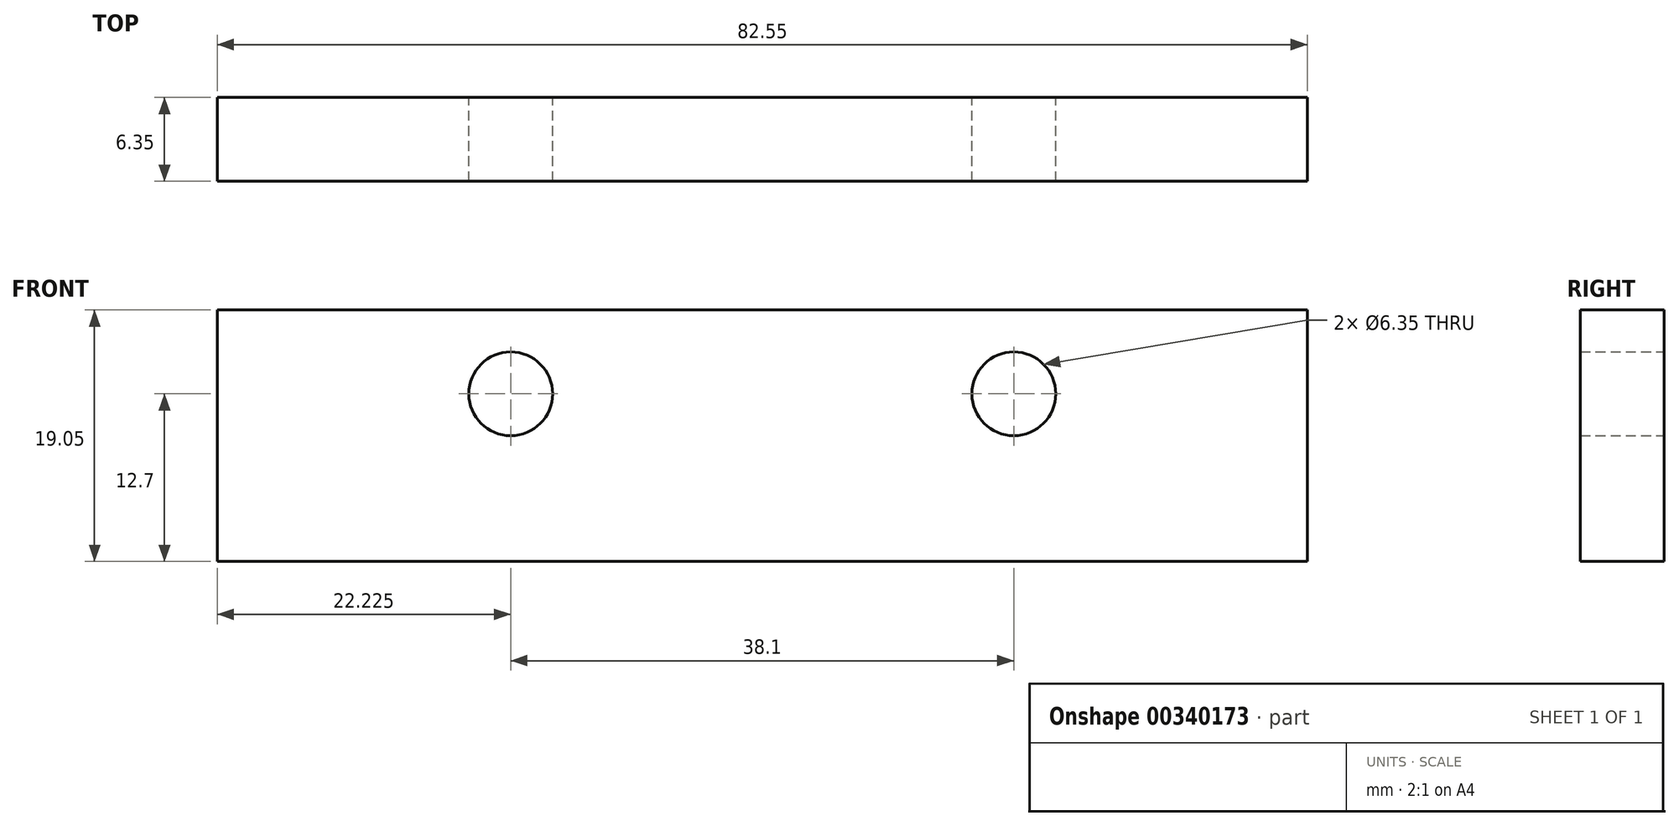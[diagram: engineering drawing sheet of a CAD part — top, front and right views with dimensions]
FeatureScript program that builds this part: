
annotation { "Feature Type Name" : "Feature", "Feature Type Description" : "" }
export const myFeature = defineFeature(function(context is Context, id is Id, definition is map)
    precondition{}
    {
        {
            var Q0;
            Q0=qCreatedBy(makeId("Front.planeOp"),FACE);
            var sketch = newSketch(context, id + "F0", { "sketchPlane" : qUnion([Q0])});
            skLineSegment(sketch, "E0.bottom", {"start": v(0, 0) * mm, "end": v(82.55, 0) * mm});
            skLineSegment(sketch, "E0.top", {"start": v(0, 19.05) * mm, "end": v(82.55, 19.05) * mm});
            skLineSegment(sketch, "E0.left", {"start": v(0, 0) * mm, "end": v(0, 19.05) * mm});
            skLineSegment(sketch, "E0.right", {"start": v(82.55, 0) * mm, "end": v(82.55, 19.05) * mm});
            skCircle(sketch, "E1", {"center": v(22.22, 12.7) * mm, "radius": 3.17 * mm});
            skCircle(sketch, "E2", {"center": v(60.33, 12.7) * mm, "radius": 3.18 * mm});
            skSolve(sketch);
        }
        {
            var Q0;
            Q0 = qSketchRegion(id + "F0", true);
            extrude(context, id + "F1", {"entities" : qUnion([Q0]), "depth" : 6.35 * mm});
        }
    });
